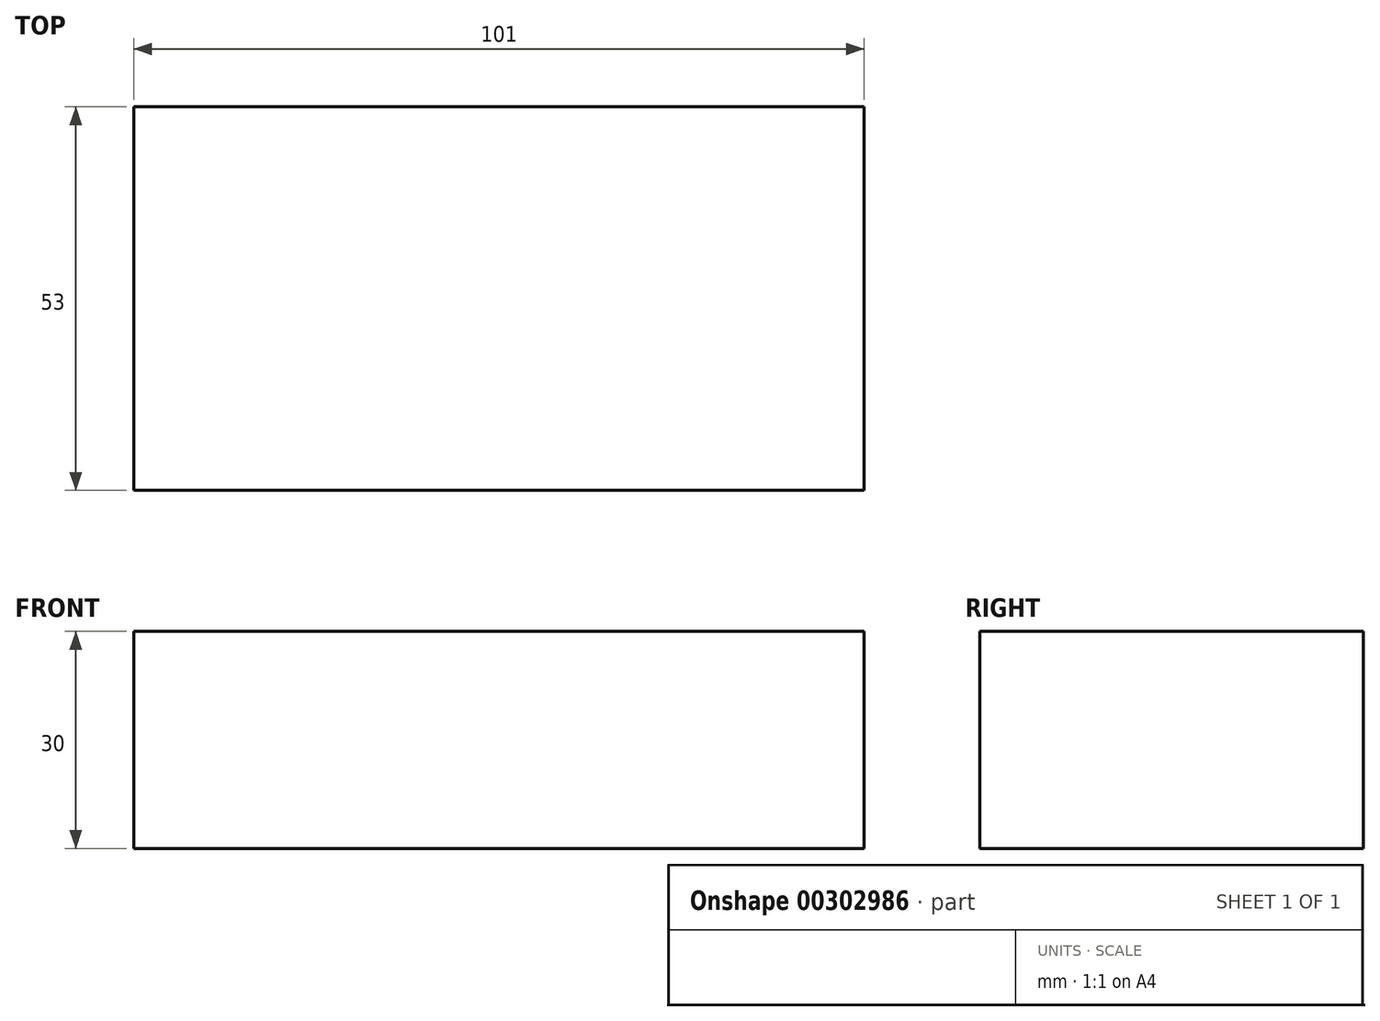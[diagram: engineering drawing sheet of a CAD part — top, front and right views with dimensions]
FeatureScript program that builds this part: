
annotation { "Feature Type Name" : "Feature", "Feature Type Description" : "" }
export const myFeature = defineFeature(function(context is Context, id is Id, definition is map)
    precondition{}
    {
        {
            var Q0;
            Q0=qCreatedBy(makeId("Top.planeOp"),FACE);
            var sketch = newSketch(context, id + "F0", { "sketchPlane" : qUnion([Q0])});
            skLineSegment(sketch, "E0.bottom", {"start": v(-41.05, 25.85) * mm, "end": v(59.95, 25.85) * mm});
            skLineSegment(sketch, "E0.top", {"start": v(-41.05, -27.15) * mm, "end": v(59.95, -27.15) * mm});
            skLineSegment(sketch, "E0.left", {"start": v(-41.05, 25.85) * mm, "end": v(-41.05, -27.15) * mm});
            skLineSegment(sketch, "E0.right", {"start": v(59.95, 25.85) * mm, "end": v(59.95, -27.15) * mm});
            skSolve(sketch);
        }
        {
            var Q0;
            Q0=makeQuery(id+"F0.imprint","IMPRINT",FACE,{"disambiguationData":[TD([[makeQuery(id+"F0.imprint","IMPRINT",EDGE,{"derivedFrom":sQuery(id+"F0.wireOp",EDGE,"E0.bottom")}),-1.0]])]});
            extrude(context, id + "F1", {"entities" : qUnion([Q0]), "depth" : 30 * mm});
        }
    });
